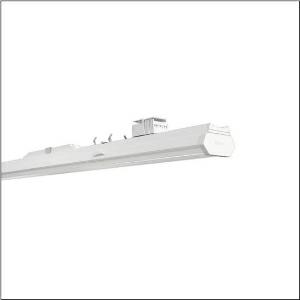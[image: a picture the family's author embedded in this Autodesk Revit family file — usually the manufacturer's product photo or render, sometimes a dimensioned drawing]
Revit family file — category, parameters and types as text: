
# Revit family: licross_r__11_protected_mo_51td1bdn49xg3s_1df8
name_source: partatom
category: Lighting Fixtures
units: mm (PartAtom-declared; Revit-internal decimal feet)

## family parameters
Cut with Voids When Loaded = No
Host = Face
Light Source = No
Part Type = Normal
Room Calculation Point = No
Round Connector Dimension = Use Diameter
Shared = No

## types (1)
- --- (1 x LED, 920 lm, 6.8 W, 4000K)
    Apparent Load = 7 VA
    CIE Flux Codes = 54 82 95 97 100
    Color Rendering = 80
    Color Temperature = 4000K
    Default Elevation = 1800 mm
    Description = Licross® 11 Protected MO, luminaire insert, of sheet steel, galvanised, coil coated, white, length: 1.500mm, width: 90mm, height: 101mm, LED rated luminous flux: 9.370lm, light colour: 840, control gear: DALI 2 (for two DALI lines), with plug, 6-pole, with phase selection, for trunking rail, 14-core, mains connection: 220..240V, AC, 50/60Hz, rated input power: 61W, for trunking rail, 14-core, halogen-free wiring, for emergency light function, converter,control gear: single battery element, battery: LiFePO4, 9Ah, primary optical cover: cover, of PMMA, light emission: direct distribution, primary light characteristic: symmetric, protection rating (complete): IP54, insulation class (complete): insulation class I (protective earthing), certification: CE, UKCA, protection symbol: D if used in an environment with non-conductive dust loads with corresponding accessories, impact resistance: IK06, permissible ambient temperature for indoor applications: +5..+35°C, standard: EN 60598-2-22, LABS conformity tested according to VDMA 24364:2018-05, reducing of maximum allowable ambient temperature of 5°C with ceiling mounting, corresponds to IFS (International Featured Standards) requirements for safety and quality in the food industry, packaging unit: 1 piece
    Height = 92 mm
    Lamp = 1 x LED
    Lamp Light Flux = 920 lm
    Lamp Power = 6.8 W
    Lamp count = 1
    Length = 1500 mm
    Luminous efficacy = 135 lm/W
    Manufacturer = Siteco
    ModVariant = No
    Model = 51TD1BDN49XG3S
    Mounting Place = Ceiling
    Mounting Type = Pendant
    Number of Poles = 1
    OnlyDefault = Yes
    Power Factor = 1
    Product Name = Licross® 11 Protected MO
    Product group = luminaire insert
    ProductGroupID = 902
    Protection Class = Protection class I
    Protection Degree = IP 54
    RLX_Detail_Level = 1
    RLX_Emergency_Light_Flux = 0 lm
    RLX_Emergency_Type = 0
    RLX_Emergency_Type_DB = No
    RlxData = <blob elided: 24681 chars, md5=ae546685>
    Socket = socket
    Standby Power = 0 W
    System Light Flux = 920 lm
    System Power = 7 W
    Type Comments = : emergency light operation: 3 h
    Type Image = l_1256145.jpg
    URL = http://relux.com
    VarID = @adj_091124
    Voltage = 0 V
    Weight = 0.00 kg
    Width = 88 mm

## geometry (parser evidence)
native form markers: Blend x4, Sweep x9
no freeform markers — native parametric forms only
